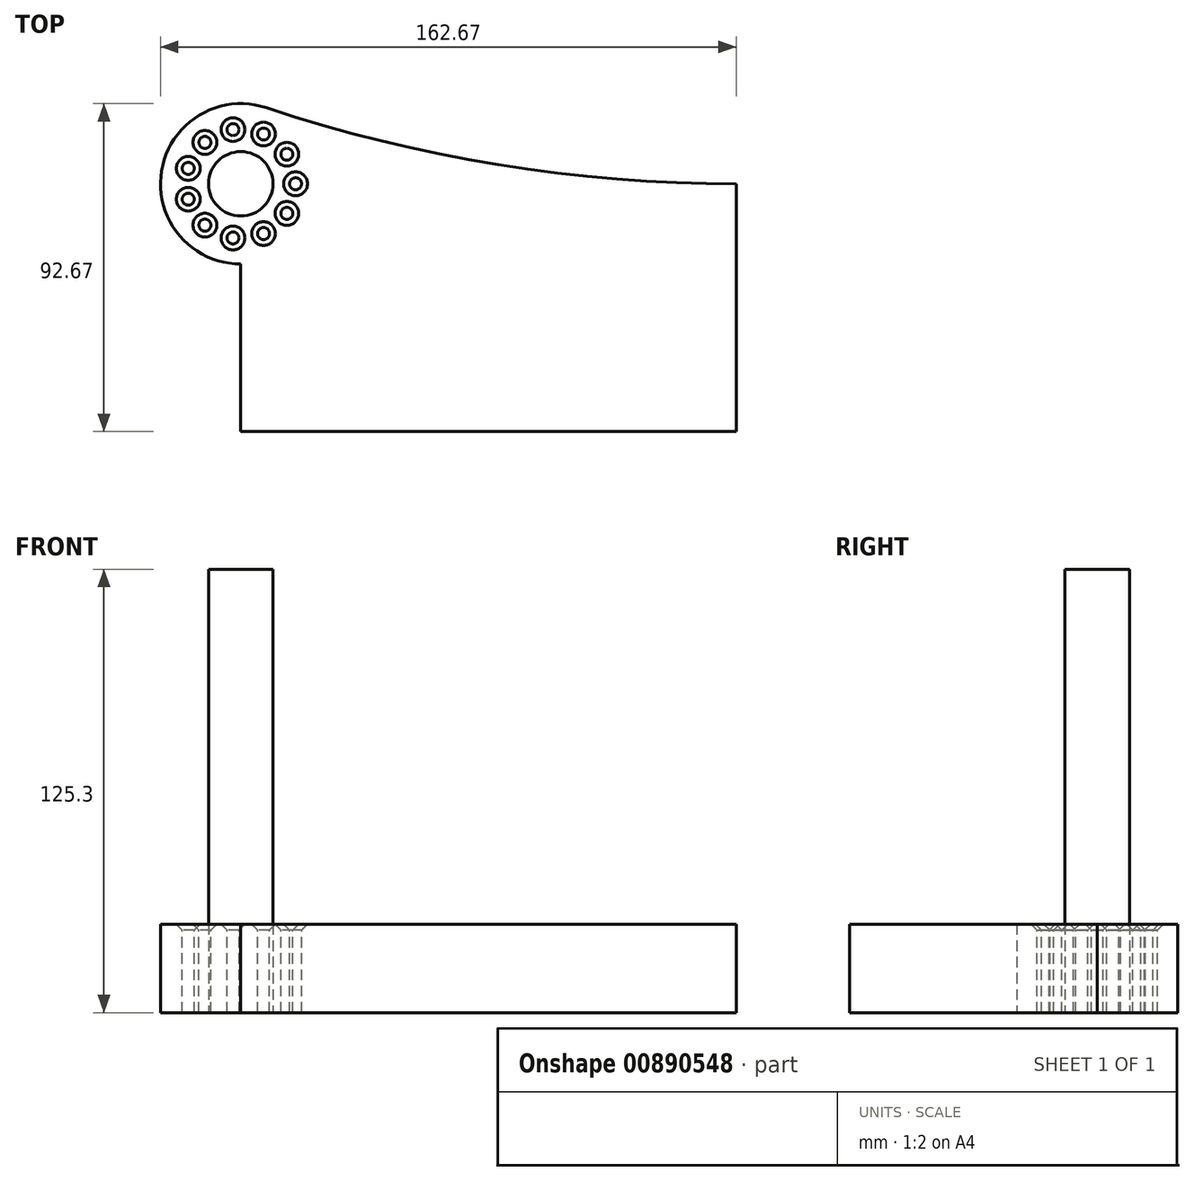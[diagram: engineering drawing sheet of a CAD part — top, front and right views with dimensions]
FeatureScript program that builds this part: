
annotation { "Feature Type Name" : "Feature", "Feature Type Description" : "" }
export const myFeature = defineFeature(function(context is Context, id is Id, definition is map)
    precondition{}
    {
        {
            var Q0;
            Q0=qCreatedBy(makeId("Top.planeOp"),FACE);
            var sketch = newSketch(context, id + "F0", { "sketchPlane" : qUnion([Q0])});
            skLineSegment(sketch, "E0.bottom", {"start": v(70, -35) * mm, "end": v(-70, -35) * mm});
            skLineSegment(sketch, "E0.top", {"start": v(70, 35) * mm, "end": v(-70, 35) * mm});
            skLineSegment(sketch, "E0.left", {"start": v(70, -35) * mm, "end": v(70, 35) * mm});
            skLineSegment(sketch, "E0.right", {"start": v(-70, -35) * mm, "end": v(-70, 35) * mm});
            skPoint(sketch, "E0.middle", {"position": v(0, 0) * mm});
            skCircle(sketch, "E1", {"center": v(-70, 35) * mm, "radius": 22.67 * mm});
            skArc(sketch, "E2", {"start": v(-62.84, 56.52) * mm, "mid": v(2.71, 40.41) * mm, "end": v(70, 35) * mm});
            skCircle(sketch, "E3", {"center": v(-70, 35) * mm, "radius": 9.1 * mm});
            skSolve(sketch);
        }
        {
            var Q0;
            {var subQ0=sQuery(id+"F0.wireOp",EDGE,"E1");var subQ4=sQuery(id+"F0.wireOp",EDGE,"E0.top");var subQ5=makeQuery(id+"F0.imprint","INTERSECT",VERTEX,{"derivedFrom":[subQ4,subQ0]});Q0=makeQuery(id+"F0.imprint","IMPRINT",FACE,{"disambiguationData":[TD([[makeQuery(id+"F0.imprint","IMPRINT",EDGE,{"disambiguationData":[TD([[subQ5,-1.0]])],"derivedFrom":subQ4}),-1.0]])]});}
            var Q1;
            {var subQ0=sQuery(id+"F0.wireOp",EDGE,"E1");var subQ1=sQuery(id+"F0.wireOp",EDGE,"E0.top");var subQ2=makeQuery(id+"F0.imprint","INTERSECT",VERTEX,{"derivedFrom":[subQ1,subQ0]});Q1=makeQuery(id+"F0.imprint","IMPRINT",FACE,{"disambiguationData":[TD([[makeQuery(id+"F0.imprint","IMPRINT",EDGE,{"disambiguationData":[TD([[subQ2,-1.0]])],"derivedFrom":subQ1}),1.0]])]});}
            var Q2;
            {var subQ5=sQuery(id+"F0.wireOp",EDGE,"E0.bottom");Q2=makeQuery(id+"F0.imprint","IMPRINT",FACE,{"disambiguationData":[TD([[makeQuery(id+"F0.imprint","IMPRINT",EDGE,{"derivedFrom":subQ5}),-1.0]])]});}
            var Q3;
            {var subQ0=sQuery(id+"F0.wireOp",EDGE,"E2");Q3=makeQuery(id+"F0.imprint","IMPRINT",FACE,{"disambiguationData":[TD([[makeQuery(id+"F0.imprint","IMPRINT",EDGE,{"derivedFrom":subQ0}),-1.0]])]});}
            extrude(context, id + "F1", {"entities" : qUnion([Q0, Q1, Q2, Q3]), "depth" : 25 * mm, "offsetDistance" : 25 * mm});
        }
        {
            var Q0;
            {var subQ0=sQuery(id+"F0.wireOp",EDGE,"E0.right");var subQ1=sQuery(id+"F0.wireOp",EDGE,"E0.top");var subQ2=makeQuery(id+"F0.imprint","INTERSECT",VERTEX,{"derivedFrom":[subQ1,subQ0]});Q0=makeQuery(id+"F0.imprint","IMPRINT",FACE,{"disambiguationData":[TD([[makeQuery(id+"F0.imprint","IMPRINT",EDGE,{"disambiguationData":[TD([[subQ2,1.0]])],"derivedFrom":subQ1}),-1.0]])]});}
            var Q1;
            {var subQ0=sQuery(id+"F0.wireOp",EDGE,"E0.right");var subQ1=sQuery(id+"F0.wireOp",EDGE,"E0.top");var subQ2=makeQuery(id+"F0.imprint","INTERSECT",VERTEX,{"derivedFrom":[subQ1,subQ0]});Q1=makeQuery(id+"F0.imprint","IMPRINT",FACE,{"disambiguationData":[TD([[makeQuery(id+"F0.imprint","IMPRINT",EDGE,{"disambiguationData":[TD([[subQ2,1.0]])],"derivedFrom":subQ1}),1.0]])]});}
            extrude(context, id + "F2", {"entities" : qUnion([Q0, Q1]), "depth" : 125.3 * mm, "offsetDistance" : 25 * mm});
        }
        {
            var Q0;
            Q0=makeQuery(id+"F1.opExtrude","CAP_FACE",FACE,{"disambiguationData":[OSD([sQuery(id+"F0.wireOp",EDGE,"E0.bottom"),sQuery(id+"F0.wireOp",EDGE,"E0.left"),sQuery(id+"F0.wireOp",EDGE,"E0.right"),sQuery(id+"F0.wireOp",EDGE,"E1"),sQuery(id+"F0.wireOp",EDGE,"E2"),sQuery(id+"F0.wireOp",EDGE,"E3")])],"isStart":false});
            var sketch = newSketch(context, id + "F3", { "sketchPlane" : qUnion([Q0])});
            skLineSegment(sketch, "E4.0", {"start": v(70, 35) * mm, "end": v(-70, 35) * mm, "construction": true});
            skPoint(sketch, "E5", {"position": v(-54.53, 35) * mm});
            skPoint(sketch, "E6.1.0", {"position": v(-56.98, 43.37) * mm});
            skPoint(sketch, "E6.2.0", {"position": v(-63.57, 49.07) * mm});
            skPoint(sketch, "E6.3.0", {"position": v(-72.2, 50.32) * mm});
            skPoint(sketch, "E6.4.0", {"position": v(-80.13, 46.7) * mm});
            skPoint(sketch, "E6.5.0", {"position": v(-84.85, 39.36) * mm});
            skPoint(sketch, "E6.6.0", {"position": v(-84.85, 30.64) * mm});
            skPoint(sketch, "E6.7.0", {"position": v(-80.13, 23.3) * mm});
            skPoint(sketch, "E6.8.0", {"position": v(-72.2, 19.68) * mm});
            skPoint(sketch, "E6.9.0", {"position": v(-63.57, 20.93) * mm});
            skPoint(sketch, "E6.10.0", {"position": v(-56.98, 26.63) * mm});
            skPoint(sketch, "E6.center", {"position": v(-70, 35) * mm});
            skSolve(sketch);
        }
        {
            var Q0;
            Q0=sQuery(id+"F3.wireOp",VERTEX,"E6.3.0");
            var Q1;
            Q1=sQuery(id+"F3.wireOp",VERTEX,"E6.2.0");
            var Q2;
            Q2=sQuery(id+"F3.wireOp",VERTEX,"E6.4.0");
            var Q3;
            Q3=sQuery(id+"F3.wireOp",VERTEX,"E6.1.0");
            var Q4;
            Q4=sQuery(id+"F3.wireOp",VERTEX,"E5");
            var Q5;
            Q5=sQuery(id+"F3.wireOp",VERTEX,"E6.10.0");
            var Q6;
            Q6=sQuery(id+"F3.wireOp",VERTEX,"E6.9.0");
            var Q7;
            Q7=sQuery(id+"F3.wireOp",VERTEX,"E6.8.0");
            var Q8;
            Q8=sQuery(id+"F3.wireOp",VERTEX,"E6.7.0");
            var Q9;
            Q9=sQuery(id+"F3.wireOp",VERTEX,"E6.6.0");
            var Q10;
            Q10=sQuery(id+"F3.wireOp",VERTEX,"E6.5.0");
            var Q11;
            Q11=makeQuery(id+"F1.opExtrude","SWEPT_BODY",BODY,{"disambiguationData":[OSD([sQuery(id+"F0.wireOp",EDGE,"E0.bottom"),sQuery(id+"F0.wireOp",EDGE,"E0.left"),sQuery(id+"F0.wireOp",EDGE,"E0.right"),sQuery(id+"F0.wireOp",EDGE,"E1"),sQuery(id+"F0.wireOp",EDGE,"E2"),sQuery(id+"F0.wireOp",EDGE,"E3")])]});
            hole(context, id + "F4", {"style" : HoleStyle.C_SINK, "endStyle" : HoleEndStyle.THROUGH, "standardTappedOrClearance" : lookupTablePath({ "fit" : "Normal", "standard" : "ISO", "size" : "M3", "type" : "Clearance" }), "standardBlindInLast" : lookupTablePath({ "fit" : "Normal", "standard" : "ISO", "size" : "M3", "type" : "Clearance" }), "holeDiameter" : 3.4 * mm, "cSinkDiameter" : 6.72 * mm, "cSinkAngle" : 90 * degree, "majorDiameter" : 5 * mm, "isTappedThrough" : true, "tappedDepth" : 12 * mm, "tapClearance" : 3, "locations" : qUnion([Q0, Q1, Q2, Q3, Q4, Q5, Q6, Q7, Q8, Q9, Q10]), "scope" : qUnion([Q11])});
        }
    });
